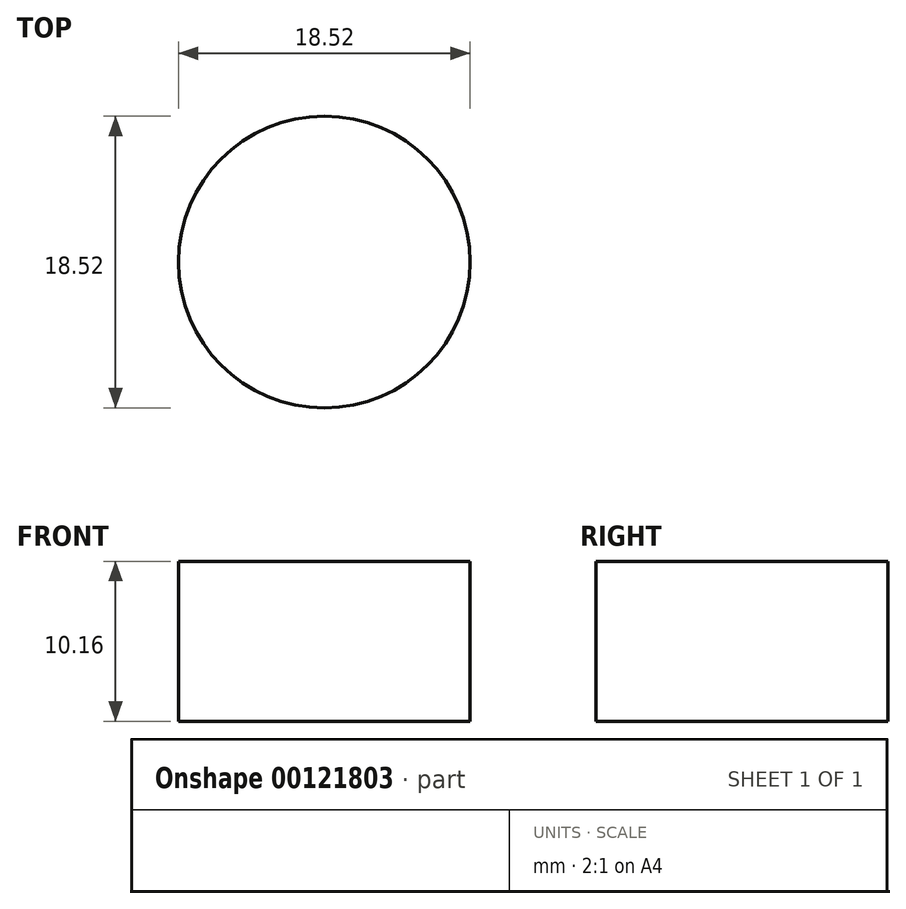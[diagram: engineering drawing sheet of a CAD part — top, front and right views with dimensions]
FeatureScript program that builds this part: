
annotation { "Feature Type Name" : "Feature", "Feature Type Description" : "" }
export const myFeature = defineFeature(function(context is Context, id is Id, definition is map)
    precondition{}
    {
        {
            var Q0;
            Q0=qCreatedBy(makeId("Top.planeOp"),FACE);
            var sketch = newSketch(context, id + "F0", { "sketchPlane" : qUnion([Q0])});
            skCircle(sketch, "E0", {"center": v(0, 0) * mm, "radius": 9.26 * mm});
            skSolve(sketch);
        }
        {
            var Q0;
            Q0=makeQuery(id+"F0.imprint","IMPRINT",FACE,{"disambiguationData":[TD([[makeQuery(id+"F0.imprint","IMPRINT",EDGE,{"derivedFrom":sQuery(id+"F0.wireOp",EDGE,"E0")}),1.0]])]});
            extrude(context, id + "F1", {"entities" : qUnion([Q0]), "depth" : 10.16 * mm});
        }
    });
